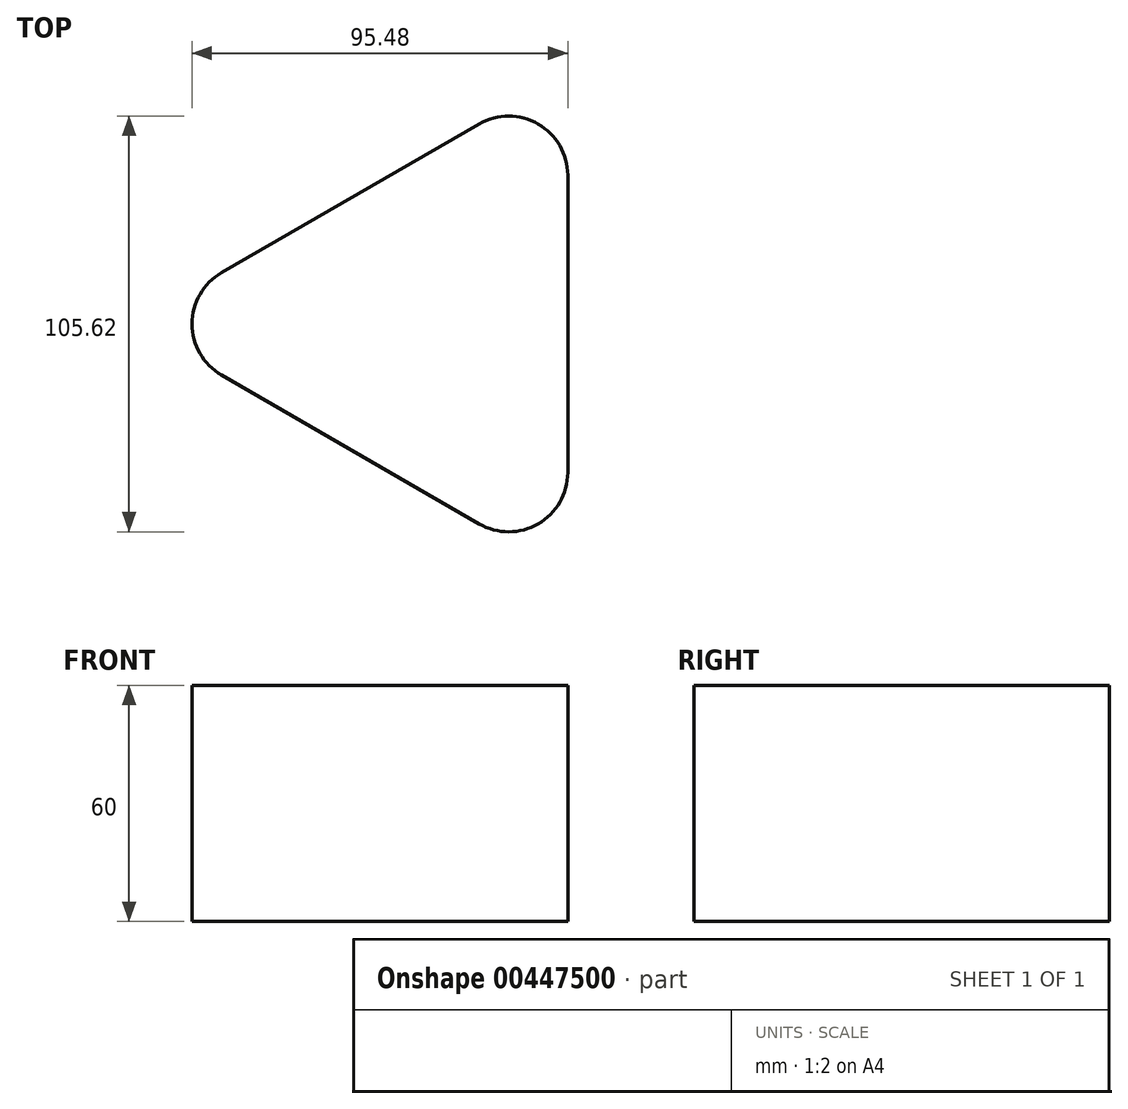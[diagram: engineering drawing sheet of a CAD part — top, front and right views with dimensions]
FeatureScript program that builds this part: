
annotation { "Feature Type Name" : "Feature", "Feature Type Description" : "" }
export const myFeature = defineFeature(function(context is Context, id is Id, definition is map)
    precondition{}
    {
        {
            var Q0;
            Q0=qCreatedBy(makeId("Top.planeOp"),FACE);
            var sketch = newSketch(context, id + "F0", { "sketchPlane" : qUnion([Q0])});
            skCircle(sketch, "E0.cCircle", {"center": v(0, 0) * mm, "radius": 36.83 * mm, "construction": true});
            skLineSegment(sketch, "E0.0", {"start": v(36.83, 63.79) * mm, "end": v(36.83, -63.79) * mm});
            skLineSegment(sketch, "E0.1", {"start": v(36.83, -63.79) * mm, "end": v(-73.65, 0) * mm});
            skLineSegment(sketch, "E0.2", {"start": v(-73.65, 0) * mm, "end": v(36.83, 63.79) * mm});
            skPoint(sketch, "E0.0.midPoint", {"position": v(36.83, 0) * mm});
            skSolve(sketch);
        }
        {
            var Q0;
            Q0 = qSketchRegion(id + "F0", true);
            extrude(context, id + "F1", {"entities" : qUnion([Q0]), "depth" : 60 * mm});
        }
        {
            var Q0;
            Q0=makeQuery(id+"F1.opExtrude","SWEPT_EDGE",EDGE,{"disambiguationData":[OSD([sQuery(id+"F0.wireOp",EDGE,"E0.0"),sQuery(id+"F0.wireOp",EDGE,"E0.2")])]});
            var Q1;
            Q1=makeQuery(id+"F1.opExtrude","SWEPT_EDGE",EDGE,{"disambiguationData":[OSD([sQuery(id+"F0.wireOp",EDGE,"E0.0"),sQuery(id+"F0.wireOp",EDGE,"E0.1")])]});
            var Q2;
            Q2=makeQuery(id+"F1.opExtrude","SWEPT_EDGE",EDGE,{"disambiguationData":[OSD([sQuery(id+"F0.wireOp",EDGE,"E0.1"),sQuery(id+"F0.wireOp",EDGE,"E0.2")])]});
            fillet(context, id + "F2", {"entities" : qUnion([Q0, Q1, Q2]), "radius" : 15 * mm, "tangentPropagation" : true, "allowEdgeOverflow" : false});
        }
    });
